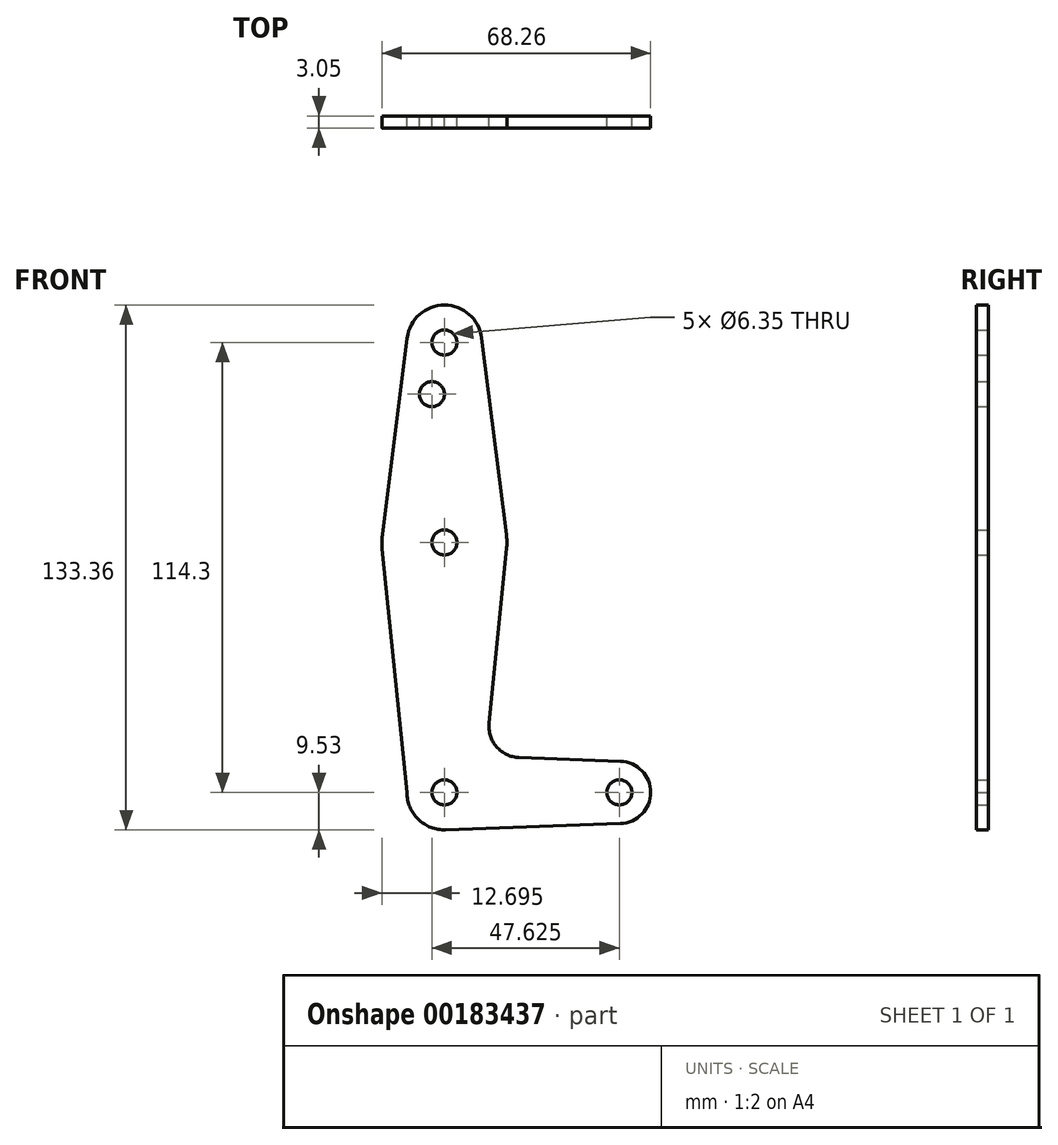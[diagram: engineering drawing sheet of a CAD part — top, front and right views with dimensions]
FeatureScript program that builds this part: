
annotation { "Feature Type Name" : "Feature", "Feature Type Description" : "" }
export const myFeature = defineFeature(function(context is Context, id is Id, definition is map)
    precondition{}
    {
        {
            var Q0;
            Q0=qCreatedBy(makeId("Front.planeOp"),FACE);
            var sketch = newSketch(context, id + "F0", { "sketchPlane" : qUnion([Q0])});
            skCircle(sketch, "E0", {"center": v(0, 0) * mm, "radius": 9.53 * mm});
            skLineSegment(sketch, "E1", {"start": v(0, 0) * mm, "end": v(44.45, 0) * mm, "construction": true});
            skLineSegment(sketch, "E2", {"start": v(0, 0) * mm, "end": v(0, 114.3) * mm, "construction": true});
            skCircle(sketch, "E3", {"center": v(44.45, 0) * mm, "radius": 7.94 * mm});
            skCircle(sketch, "E4", {"center": v(0, 114.3) * mm, "radius": 9.53 * mm});
            skCircle(sketch, "E5", {"center": v(0, 63.5) * mm, "radius": 15.88 * mm});
            skLineSegment(sketch, "E6", {"start": v(-9.45, 115.5) * mm, "end": v(-15.75, 65.48) * mm});
            skLineSegment(sketch, "E7", {"start": v(9.45, 115.5) * mm, "end": v(15.75, 65.48) * mm});
            skLineSegment(sketch, "E8", {"start": v(-9.52, 0) * mm, "end": v(-15.8, 61.9) * mm});
            skLineSegment(sketch, "E9", {"start": v(11.34, 17.6) * mm, "end": v(15.8, 61.91) * mm});
            skLineSegment(sketch, "E10", {"start": v(0.34, -9.52) * mm, "end": v(44.73, -7.93) * mm});
            skLineSegment(sketch, "E11", {"start": v(18.97, 8.85) * mm, "end": v(44.73, 7.93) * mm});
            skCircle(sketch, "E12", {"center": v(0, 114.3) * mm, "radius": 3.18 * mm});
            skCircle(sketch, "E13", {"center": v(-3.18, 101.17) * mm, "radius": 3.18 * mm});
            skCircle(sketch, "E14", {"center": v(0, 63.5) * mm, "radius": 3.18 * mm});
            skCircle(sketch, "E15", {"center": v(0, 0) * mm, "radius": 3.18 * mm});
            skCircle(sketch, "E16", {"center": v(44.45, 0) * mm, "radius": 3.18 * mm});
            skArc(sketch, "E17.filletArc", {"start": v(11.34, 17.6) * mm, "mid": v(13.26, 11.57) * mm, "end": v(18.97, 8.85) * mm});
            skSolve(sketch);
        }
        {
            var Q0;
            Q0=makeQuery(id+"F0.imprint","IMPRINT",FACE,{"disambiguationData":[TD([[makeQuery(id+"F0.imprint","IMPRINT",EDGE,{"derivedFrom":sQuery(id+"F0.wireOp",EDGE,"E15")}),-1.0]])]});
            var Q1;
            Q1=makeQuery(id+"F0.imprint","IMPRINT",FACE,{"disambiguationData":[TD([[makeQuery(id+"F0.imprint","IMPRINT",EDGE,{"derivedFrom":sQuery(id+"F0.wireOp",EDGE,"E16")}),-1.0]])]});
            var Q2;
            Q2=makeQuery(id+"F0.imprint","IMPRINT",FACE,{"disambiguationData":[TD([[makeQuery(id+"F0.imprint","IMPRINT",EDGE,{"derivedFrom":sQuery(id+"F0.wireOp",EDGE,"E12")}),-1.0]])]});
            var Q3;
            {var subQ0=sQuery(id+"F0.wireOp",EDGE,"E8");Q3=makeQuery(id+"F0.imprint","IMPRINT",FACE,{"disambiguationData":[TD([[makeQuery(id+"F0.imprint","IMPRINT",EDGE,{"derivedFrom":subQ0}),-1.0]])]});}
            var Q4;
            Q4=makeQuery(id+"F0.imprint","IMPRINT",FACE,{"disambiguationData":[TD([[makeQuery(id+"F0.imprint","IMPRINT",EDGE,{"derivedFrom":sQuery(id+"F0.wireOp",EDGE,"E14")}),-1.0]])]});
            var Q5;
            {var subQ1=sQuery(id+"F0.wireOp",EDGE,"E6");Q5=makeQuery(id+"F0.imprint","IMPRINT",FACE,{"disambiguationData":[TD([[makeQuery(id+"F0.imprint","IMPRINT",EDGE,{"derivedFrom":subQ1}),1.0]])]});}
            extrude(context, id + "F1", {"entities" : qUnion([Q0, Q1, Q2, Q3, Q4, Q5]), "depth" : 3.05 * mm});
        }
    });
